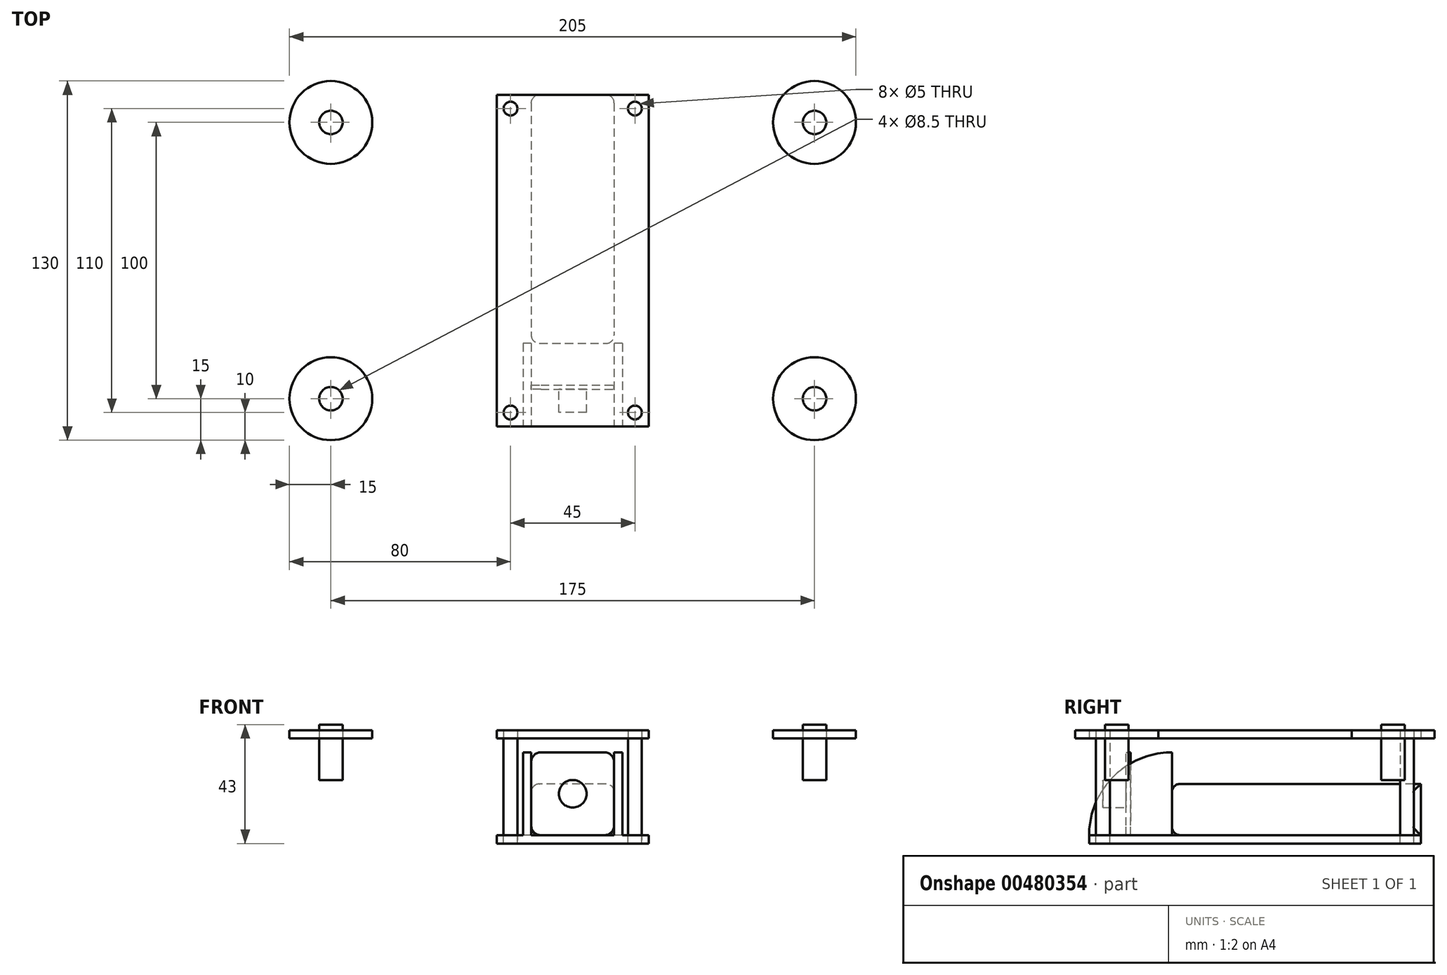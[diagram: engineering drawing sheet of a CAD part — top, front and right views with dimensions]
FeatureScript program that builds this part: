
annotation { "Feature Type Name" : "Feature", "Feature Type Description" : "" }
export const myFeature = defineFeature(function(context is Context, id is Id, definition is map)
    precondition{}
    {
        {
            var Q0;
            Q0=qCreatedBy(makeId("Top.planeOp"),FACE);
            var sketch = newSketch(context, id + "F0", { "sketchPlane" : qUnion([Q0])});
            skLineSegment(sketch, "E0.bottom", {"start": v(27.5, -60) * mm, "end": v(-27.5, -60) * mm});
            skLineSegment(sketch, "E0.top", {"start": v(27.5, 60) * mm, "end": v(-27.5, 60) * mm});
            skLineSegment(sketch, "E0.left", {"start": v(27.5, -60) * mm, "end": v(27.5, 60) * mm});
            skLineSegment(sketch, "E0.right", {"start": v(-27.5, -60) * mm, "end": v(-27.5, 60) * mm});
            skPoint(sketch, "E0.middle", {"position": v(0, 0) * mm});
            skLineSegment(sketch, "E1", {"start": v(-27.5, 60) * mm, "end": v(-27.5, 55) * mm});
            skLineSegment(sketch, "E2", {"start": v(-27.5, 55) * mm, "end": v(-22.5, 55) * mm, "construction": true});
            skLineSegment(sketch, "E3", {"start": v(-22.5, 55) * mm, "end": v(22.5, 55) * mm, "construction": true});
            skLineSegment(sketch, "E4", {"start": v(22.5, 55) * mm, "end": v(22.5, -55) * mm, "construction": true});
            skLineSegment(sketch, "E5", {"start": v(22.5, -55) * mm, "end": v(-22.5, -55) * mm, "construction": true});
            skCircle(sketch, "E6", {"center": v(-22.5, 55) * mm, "radius": 2.5 * mm});
            skCircle(sketch, "E7", {"center": v(22.5, 55) * mm, "radius": 2.5 * mm});
            skCircle(sketch, "E8", {"center": v(22.5, -55) * mm, "radius": 2.5 * mm});
            skCircle(sketch, "E9", {"center": v(-22.5, -55) * mm, "radius": 2.5 * mm});
            skLineSegment(sketch, "E10", {"start": v(0, 60) * mm, "end": v(-15, 60) * mm});
            skLineSegment(sketch, "E11.bottom", {"start": v(-15, 60) * mm, "end": v(15, 60) * mm});
            skLineSegment(sketch, "E11.top", {"start": v(-15, -30) * mm, "end": v(15, -30) * mm});
            skLineSegment(sketch, "E11.left", {"start": v(-15, 60) * mm, "end": v(-15, -30) * mm});
            skLineSegment(sketch, "E11.right", {"start": v(15, 60) * mm, "end": v(15, -30) * mm});
            skSolve(sketch);
        }
        {
            var Q0;
            Q0=qCreatedBy(makeId("Top.planeOp"),FACE);
            cPlane(context, id + "F1", {"entities" : qUnion([Q0]), "cplaneType" : CPlaneType.OFFSET, "offset" : 35 * mm, "width" : 150 * mm, "height" : 150 * mm});
        }
        {
            var Q0;
            Q0=qCreatedBy(id+"F1.planeOp",FACE);
            var sketch = newSketch(context, id + "F2", { "sketchPlane" : qUnion([Q0])});
            skLineSegment(sketch, "E12.bottom", {"start": v(27.5, -60) * mm, "end": v(-27.5, -60) * mm});
            skLineSegment(sketch, "E12.top", {"start": v(27.5, 60) * mm, "end": v(-27.5, 60) * mm});
            skLineSegment(sketch, "E12.left", {"start": v(27.5, -60) * mm, "end": v(27.5, 60) * mm});
            skLineSegment(sketch, "E12.right", {"start": v(-27.5, -60) * mm, "end": v(-27.5, 60) * mm});
            skPoint(sketch, "E12.middle", {"position": v(0, 0) * mm});
            skLineSegment(sketch, "E13.bottom", {"start": v(-27.5, 60) * mm, "end": v(-87.5, 60) * mm});
            skLineSegment(sketch, "E13.top", {"start": v(-27.5, 40) * mm, "end": v(-87.5, 40) * mm});
            skLineSegment(sketch, "E13.left", {"start": v(-27.5, 60) * mm, "end": v(-27.5, 40) * mm});
            skLineSegment(sketch, "E13.right", {"start": v(-87.5, 60) * mm, "end": v(-87.5, 40) * mm, "construction": true});
            skLineSegment(sketch, "E14.bottom", {"start": v(27.5, 60) * mm, "end": v(87.5, 60) * mm});
            skLineSegment(sketch, "E14.top", {"start": v(27.5, 40) * mm, "end": v(87.5, 40) * mm});
            skLineSegment(sketch, "E14.left", {"start": v(27.5, 60) * mm, "end": v(27.5, 40) * mm});
            skLineSegment(sketch, "E14.right", {"start": v(87.5, 60) * mm, "end": v(87.5, 40) * mm, "construction": true});
            skLineSegment(sketch, "E15.bottom", {"start": v(27.5, -60) * mm, "end": v(87.5, -60) * mm});
            skLineSegment(sketch, "E15.top", {"start": v(27.5, -40) * mm, "end": v(87.5, -40) * mm});
            skLineSegment(sketch, "E15.left", {"start": v(27.5, -60) * mm, "end": v(27.5, -40) * mm});
            skLineSegment(sketch, "E15.right", {"start": v(87.5, -60) * mm, "end": v(87.5, -40) * mm, "construction": true});
            skLineSegment(sketch, "E16.bottom", {"start": v(-27.5, -60) * mm, "end": v(-87.5, -60) * mm});
            skLineSegment(sketch, "E16.top", {"start": v(-27.5, -40) * mm, "end": v(-87.5, -40) * mm});
            skLineSegment(sketch, "E16.left", {"start": v(-27.5, -60) * mm, "end": v(-27.5, -40) * mm});
            skLineSegment(sketch, "E16.right", {"start": v(-87.5, -60) * mm, "end": v(-87.5, -40) * mm, "construction": true});
            skCircle(sketch, "E17", {"center": v(-87.5, -50) * mm, "radius": 15 * mm});
            skCircle(sketch, "E18", {"center": v(-87.5, 50) * mm, "radius": 15 * mm});
            skCircle(sketch, "E19", {"center": v(87.5, 50) * mm, "radius": 15 * mm});
            skCircle(sketch, "E20", {"center": v(87.5, -50) * mm, "radius": 15 * mm});
            skCircle(sketch, "E21", {"center": v(-87.5, 50) * mm, "radius": 4.25 * mm});
            skCircle(sketch, "E22", {"center": v(87.5, 50) * mm, "radius": 4.25 * mm});
            skCircle(sketch, "E23", {"center": v(87.5, -50) * mm, "radius": 4.25 * mm});
            skCircle(sketch, "E24", {"center": v(-87.5, -50) * mm, "radius": 4.25 * mm});
            skLineSegment(sketch, "E25", {"start": v(-27.5, 60) * mm, "end": v(-27.5, 55) * mm});
            skLineSegment(sketch, "E26", {"start": v(-27.5, 55) * mm, "end": v(-22.5, 55) * mm, "construction": true});
            skLineSegment(sketch, "E27", {"start": v(-22.5, 55) * mm, "end": v(22.5, 55) * mm, "construction": true});
            skLineSegment(sketch, "E28", {"start": v(22.5, 55) * mm, "end": v(22.5, -55) * mm, "construction": true});
            skLineSegment(sketch, "E29", {"start": v(22.5, -55) * mm, "end": v(-22.5, -55) * mm, "construction": true});
            skCircle(sketch, "E30", {"center": v(-22.5, -55) * mm, "radius": 2.5 * mm});
            skCircle(sketch, "E31", {"center": v(22.5, -55) * mm, "radius": 2.5 * mm});
            skCircle(sketch, "E32", {"center": v(22.5, 55) * mm, "radius": 2.5 * mm});
            skCircle(sketch, "E33", {"center": v(-22.5, 55) * mm, "radius": 2.5 * mm});
            skSolve(sketch);
        }
        {
            var Q0;
            {var subQ0=sQuery(id+"F2.wireOp",EDGE,"E13.left");Q0=makeQuery(id+"F2.imprint","IMPRINT",FACE,{"disambiguationData":[TD([[makeQuery(id+"F2.imprint","IMPRINT",EDGE,{"derivedFrom":subQ0}),-1.0]])]});}
            var Q1;
            Q1=makeQuery(id+"F2.imprint","IMPRINT",FACE,{"disambiguationData":[TD([[makeQuery(id+"F2.imprint","IMPRINT",EDGE,{"derivedFrom":sQuery(id+"F2.wireOp",EDGE,"E21")}),-1.0]])]});
            var Q2;
            Q2=makeQuery(id+"F2.imprint","IMPRINT",FACE,{"disambiguationData":[TD([[makeQuery(id+"F2.imprint","IMPRINT",EDGE,{"derivedFrom":sQuery(id+"F2.wireOp",EDGE,"E12.bottom")}),-1.0]])]});
            var Q3;
            {var subQ0=sQuery(id+"F2.wireOp",EDGE,"E14.left");Q3=makeQuery(id+"F2.imprint","IMPRINT",FACE,{"disambiguationData":[TD([[makeQuery(id+"F2.imprint","IMPRINT",EDGE,{"derivedFrom":subQ0}),1.0]])]});}
            var Q4;
            Q4=makeQuery(id+"F2.imprint","IMPRINT",FACE,{"disambiguationData":[TD([[makeQuery(id+"F2.imprint","IMPRINT",EDGE,{"derivedFrom":sQuery(id+"F2.wireOp",EDGE,"E22")}),-1.0]])]});
            var Q5;
            Q5=makeQuery(id+"F2.imprint","IMPRINT",FACE,{"disambiguationData":[TD([[makeQuery(id+"F2.imprint","IMPRINT",EDGE,{"derivedFrom":sQuery(id+"F2.wireOp",EDGE,"E23")}),-1.0]])]});
            var Q6;
            {var subQ0=sQuery(id+"F2.wireOp",EDGE,"E15.left");Q6=makeQuery(id+"F2.imprint","IMPRINT",FACE,{"disambiguationData":[TD([[makeQuery(id+"F2.imprint","IMPRINT",EDGE,{"derivedFrom":subQ0}),-1.0]])]});}
            var Q7;
            Q7=makeQuery(id+"F2.imprint","IMPRINT",FACE,{"disambiguationData":[TD([[makeQuery(id+"F2.imprint","IMPRINT",EDGE,{"derivedFrom":sQuery(id+"F2.wireOp",EDGE,"E24")}),-1.0]])]});
            var Q8;
            {var subQ0=sQuery(id+"F2.wireOp",EDGE,"E16.left");Q8=makeQuery(id+"F2.imprint","IMPRINT",FACE,{"disambiguationData":[TD([[makeQuery(id+"F2.imprint","IMPRINT",EDGE,{"derivedFrom":subQ0}),1.0]])]});}
            extrude(context, id + "F3", {"entities" : qUnion([Q0, Q1, Q2, Q3, Q4, Q5, Q6, Q7, Q8]), "depth" : 3 * mm});
        }
        {
            var Q0;
            Q0=makeQuery(id+"F0.imprint","IMPRINT",FACE,{"disambiguationData":[TD([[makeQuery(id+"F0.imprint","IMPRINT",EDGE,{"derivedFrom":sQuery(id+"F0.wireOp",EDGE,"E0.bottom")}),-1.0]])]});
            var Q1;
            Q1=makeQuery(id+"F0.imprint","IMPRINT",FACE,{"disambiguationData":[TD([[makeQuery(id+"F0.imprint","IMPRINT",EDGE,{"derivedFrom":sQuery(id+"F0.wireOp",EDGE,"E11.top")}),1.0]])]});
            extrude(context, id + "F4", {"entities" : qUnion([Q0, Q1]), "oppositeDirection" : true, "depth" : 3 * mm});
        }
        {
            var Q0;
            Q0=makeQuery(id+"F0.imprint","IMPRINT",FACE,{"disambiguationData":[TD([[makeQuery(id+"F0.imprint","IMPRINT",EDGE,{"derivedFrom":sQuery(id+"F0.wireOp",EDGE,"E6")}),1.0]])]});
            var Q1;
            Q1=makeQuery(id+"F0.imprint","IMPRINT",FACE,{"disambiguationData":[TD([[makeQuery(id+"F0.imprint","IMPRINT",EDGE,{"derivedFrom":sQuery(id+"F0.wireOp",EDGE,"E7")}),1.0]])]});
            var Q2;
            Q2=makeQuery(id+"F0.imprint","IMPRINT",FACE,{"disambiguationData":[TD([[makeQuery(id+"F0.imprint","IMPRINT",EDGE,{"derivedFrom":sQuery(id+"F0.wireOp",EDGE,"E8")}),1.0]])]});
            var Q3;
            Q3=makeQuery(id+"F0.imprint","IMPRINT",FACE,{"disambiguationData":[TD([[makeQuery(id+"F0.imprint","IMPRINT",EDGE,{"derivedFrom":sQuery(id+"F0.wireOp",EDGE,"E9")}),1.0]])]});
            extrude(context, id + "F5", {"entities" : qUnion([Q0, Q1, Q2, Q3]), "depth" : 38 * mm, "hasSecondDirection" : true, "secondDirectionOppositeDirection" : true, "secondDirectionDepth" : 3 * mm});
        }
        {
            var Q0;
            Q0=makeQuery(id+"F2.imprint","IMPRINT",FACE,{"disambiguationData":[TD([[makeQuery(id+"F2.imprint","IMPRINT",EDGE,{"derivedFrom":sQuery(id+"F2.wireOp",EDGE,"E24")}),1.0]])]});
            var Q1;
            Q1=makeQuery(id+"F2.imprint","IMPRINT",FACE,{"disambiguationData":[TD([[makeQuery(id+"F2.imprint","IMPRINT",EDGE,{"derivedFrom":sQuery(id+"F2.wireOp",EDGE,"E23")}),1.0]])]});
            var Q2;
            Q2=makeQuery(id+"F2.imprint","IMPRINT",FACE,{"disambiguationData":[TD([[makeQuery(id+"F2.imprint","IMPRINT",EDGE,{"derivedFrom":sQuery(id+"F2.wireOp",EDGE,"E21")}),1.0]])]});
            var Q3;
            Q3=makeQuery(id+"F2.imprint","IMPRINT",FACE,{"disambiguationData":[TD([[makeQuery(id+"F2.imprint","IMPRINT",EDGE,{"derivedFrom":sQuery(id+"F2.wireOp",EDGE,"E22")}),1.0]])]});
            extrude(context, id + "F6", {"entities" : qUnion([Q0, Q1, Q2, Q3]), "depth" : 5 * mm, "hasSecondDirection" : true, "secondDirectionOppositeDirection" : true, "secondDirectionDepth" : 15 * mm});
        }
        {
            var Q0;
            Q0=qCreatedBy(makeId("Right.planeOp"),FACE);
            var sketch = newSketch(context, id + "F7", { "sketchPlane" : qUnion([Q0])});
            skLineSegment(sketch, "E34", {"start": v(0, 0) * mm, "end": v(-30, 0) * mm, "construction": true});
            skLineSegment(sketch, "E35", {"start": v(-30, 0) * mm, "end": v(-60, 0) * mm});
            skLineSegment(sketch, "E36", {"start": v(-30, 0) * mm, "end": v(-30, 30) * mm});
            skArc(sketch, "E37", {"start": v(-60, 0) * mm, "mid": v(-51.21, 21.21) * mm, "end": v(-30, 30) * mm});
            skSolve(sketch);
        }
        {
            var Q0;
            Q0=makeQuery(id+"F7.imprint","IMPRINT",FACE,{"disambiguationData":[TD([[makeQuery(id+"F7.imprint","IMPRINT",EDGE,{"derivedFrom":sQuery(id+"F7.wireOp",EDGE,"E35")}),-1.0]])]});
            extrude(context, id + "F8", {"entities" : qUnion([Q0]), "operationType" : NewBodyOperationType.ADD, "endBound" : BoundingType.SYMMETRIC, "depth" : 36 * mm});
        }
        {
            var Q0;
            Q0=makeQuery(id+"F7.imprint","IMPRINT",FACE,{"disambiguationData":[TD([[makeQuery(id+"F7.imprint","IMPRINT",EDGE,{"derivedFrom":sQuery(id+"F7.wireOp",EDGE,"E35")}),-1.0]])]});
            extrude(context, id + "F9", {"entities" : qUnion([Q0]), "operationType" : NewBodyOperationType.REMOVE, "endBound" : BoundingType.SYMMETRIC, "oppositeDirection" : true, "depth" : 30 * mm});
        }
        {
            var Q0;
            Q0=sQuery(id+"F7.wireOp",EDGE,"E36");
            cPlane(context, id + "F10", {"entities" : qUnion([Q0]), "cplaneType" : CPlaneType.LINE_ANGLE, "offset" : 25 * mm, "angle" : 270 * degree, "width" : 150 * mm, "height" : 150 * mm});
        }
        {
            var Q0;
            Q0=qCreatedBy(id+"F10.planeOp",FACE);
            var sketch = newSketch(context, id + "F11", { "sketchPlane" : qUnion([Q0])});
            skLineSegment(sketch, "E38", {"start": v(0, 0) * mm, "end": v(15, 0) * mm});
            skLineSegment(sketch, "E39", {"start": v(15, 0) * mm, "end": v(15, 30) * mm});
            skLineSegment(sketch, "E40", {"start": v(15, 30) * mm, "end": v(-15, 30) * mm});
            skLineSegment(sketch, "E41", {"start": v(-15, 30) * mm, "end": v(-15, 0) * mm});
            skLineSegment(sketch, "E42", {"start": v(-15, 0) * mm, "end": v(0, 0) * mm});
            skLineSegment(sketch, "E43", {"start": v(0, 0) * mm, "end": v(0, 15) * mm, "construction": true});
            skCircle(sketch, "E44", {"center": v(0, 15) * mm, "radius": 5 * mm});
            skSolve(sketch);
        }
        {
            var Q0;
            Q0=makeQuery(id+"F11.imprint","IMPRINT",FACE,{"disambiguationData":[TD([[makeQuery(id+"F11.imprint","IMPRINT",EDGE,{"derivedFrom":sQuery(id+"F11.wireOp",EDGE,"E38")}),1.0]])]});
            var Q1;
            Q1=makeQuery(id+"F11.imprint","IMPRINT",FACE,{"disambiguationData":[TD([[makeQuery(id+"F11.imprint","IMPRINT",EDGE,{"derivedFrom":sQuery(id+"F11.wireOp",EDGE,"E44")}),1.0]])]});
            extrude(context, id + "F12", {"entities" : qUnion([Q0, Q1]), "depth" : 16.6 * mm, "hasSecondDirection" : true, "secondDirectionOppositeDirection" : false, "secondDirectionDepth" : 15 * mm});
        }
        {
            var Q0;
            Q0=makeQuery(id+"F11.imprint","IMPRINT",FACE,{"disambiguationData":[TD([[makeQuery(id+"F11.imprint","IMPRINT",EDGE,{"derivedFrom":sQuery(id+"F11.wireOp",EDGE,"E44")}),1.0]])]});
            extrude(context, id + "F13", {"entities" : qUnion([Q0]), "operationType" : NewBodyOperationType.ADD, "depth" : 25 * mm, "hasSecondDirection" : true, "secondDirectionOppositeDirection" : false, "secondDirectionDepth" : 15 * mm});
        }
        {
            var Q0;
            Q0=makeQuery(id+"F12.opExtrude","SWEPT_EDGE",EDGE,{"disambiguationData":[OSD([sQuery(id+"F11.wireOp",EDGE,"E41"),sQuery(id+"F11.wireOp",EDGE,"E42")])]});
            var Q1;
            Q1=makeQuery(id+"F12.opExtrude","SWEPT_EDGE",EDGE,{"disambiguationData":[OSD([sQuery(id+"F11.wireOp",EDGE,"E40"),sQuery(id+"F11.wireOp",EDGE,"E41")])]});
            var Q2;
            Q2=makeQuery(id+"F12.opExtrude","SWEPT_EDGE",EDGE,{"disambiguationData":[OSD([sQuery(id+"F11.wireOp",EDGE,"E39"),sQuery(id+"F11.wireOp",EDGE,"E40")])]});
            var Q3;
            Q3=makeQuery(id+"F12.opExtrude","SWEPT_EDGE",EDGE,{"disambiguationData":[OSD([sQuery(id+"F11.wireOp",EDGE,"E38"),sQuery(id+"F11.wireOp",EDGE,"E39")])]});
            fillet(context, id + "F14", {"entities" : qUnion([Q0, Q1, Q2, Q3]), "radius" : 3.5 * mm, "tangentPropagation" : true, "allowEdgeOverflow" : false});
        }
        {
            var Q0;
            Q0=makeQuery(id+"F0.imprint","IMPRINT",FACE,{"disambiguationData":[TD([[makeQuery(id+"F0.imprint","IMPRINT",EDGE,{"derivedFrom":sQuery(id+"F0.wireOp",EDGE,"E11.top")}),1.0]])]});
            extrude(context, id + "F15", {"entities" : qUnion([Q0]), "depth" : 18.6 * mm});
        }
        {
            var Q0;
            Q0=makeQuery(id+"F15.opExtrude","CAP_EDGE",EDGE,{"disambiguationData":[OSD([sQuery(id+"F0.wireOp",EDGE,"E11.right")])],"isStart":false});
            var Q1;
            Q1=makeQuery(id+"F15.opExtrude","CAP_EDGE",EDGE,{"disambiguationData":[OSD([sQuery(id+"F0.wireOp",EDGE,"E11.top")])],"isStart":false});
            var Q2;
            Q2=makeQuery(id+"F15.opExtrude","CAP_EDGE",EDGE,{"disambiguationData":[OSD([sQuery(id+"F0.wireOp",EDGE,"E11.left")])],"isStart":false});
            var Q3;
            Q3=makeQuery(id+"F15.opExtrude","CAP_EDGE",EDGE,{"disambiguationData":[OSD([sQuery(id+"F0.wireOp",EDGE,"E11.bottom")])],"isStart":false});
            var Q4;
            Q4=makeQuery(id+"F15.opExtrude","SWEPT_EDGE",EDGE,{"disambiguationData":[OSD([sQuery(id+"F0.wireOp",EDGE,"E0.top"),sQuery(id+"F0.wireOp",EDGE,"E11.bottom"),sQuery(id+"F0.wireOp",EDGE,"E11.left")])]});
            var Q5;
            Q5=makeQuery(id+"F15.opExtrude","SWEPT_EDGE",EDGE,{"disambiguationData":[OSD([sQuery(id+"F0.wireOp",EDGE,"E0.top"),sQuery(id+"F0.wireOp",EDGE,"E11.bottom"),sQuery(id+"F0.wireOp",EDGE,"E11.right")])]});
            var Q6;
            Q6=makeQuery(id+"F15.opExtrude","SWEPT_EDGE",EDGE,{"disambiguationData":[OSD([sQuery(id+"F0.wireOp",EDGE,"E11.top"),sQuery(id+"F0.wireOp",EDGE,"E11.right")])]});
            var Q7;
            Q7=makeQuery(id+"F15.opExtrude","CAP_EDGE",EDGE,{"disambiguationData":[OSD([sQuery(id+"F0.wireOp",EDGE,"E11.right")])],"isStart":true});
            var Q8;
            Q8=makeQuery(id+"F15.opExtrude","CAP_EDGE",EDGE,{"disambiguationData":[OSD([sQuery(id+"F0.wireOp",EDGE,"E11.bottom")])],"isStart":true});
            var Q9;
            Q9=makeQuery(id+"F15.opExtrude","CAP_EDGE",EDGE,{"disambiguationData":[OSD([sQuery(id+"F0.wireOp",EDGE,"E11.top")])],"isStart":true});
            var Q10;
            Q10=makeQuery(id+"F15.opExtrude","SWEPT_EDGE",EDGE,{"disambiguationData":[OSD([sQuery(id+"F0.wireOp",EDGE,"E11.top"),sQuery(id+"F0.wireOp",EDGE,"E11.left")])]});
            var Q11;
            Q11=makeQuery(id+"F15.opExtrude","CAP_EDGE",EDGE,{"disambiguationData":[OSD([sQuery(id+"F0.wireOp",EDGE,"E11.left")])],"isStart":true});
            fillet(context, id + "F16", {"entities" : qUnion([Q0, Q1, Q2, Q3, Q4, Q5, Q6, Q7, Q8, Q9, Q10, Q11]), "radius" : 3 * mm, "tangentPropagation" : true, "allowEdgeOverflow" : false});
        }
    });
